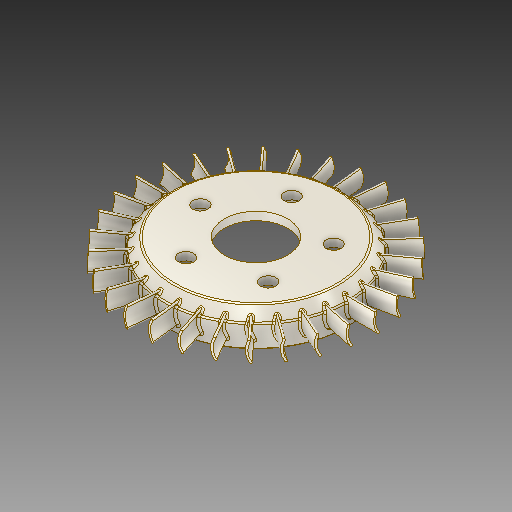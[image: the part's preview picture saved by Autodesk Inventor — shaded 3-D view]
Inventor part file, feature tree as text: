
AUTODESK INVENTOR PART (.ipt)
format: ipt  version: 2019 (Build 230136000, 136)  size: 2,094,080 bytes
history: native  units: mm
features: hole x4, sketch x4, extrude x3, fillet x3, chamfer x2, pattern_circular x2
ambient origin geometry x8: Origin, YZ Plane, XZ Plane, XY Plane, X Axis, Y Axis, Z Axis, Center Point
bodies: Solid1 (feature_tree)
feature tree (18):
  extrude  "Extrusion1"  Depth=26.0mm TaperAngle=0.0deg
  chamfer  "Chamfer1"  Distance=10.0mm
  fillet  "Fillet10"  Radius=44.0mm
  extrude  "Extrusion2"  Depth=19.5mm TaperAngle=360.0deg
  fillet  "Fillet2"  Radius=1.5mm
  pattern_circular  "Circular Pattern2"  Count=30  [1 undecoded]
  extrude  "Extrusion3"  Depth=19.5mm
  fillet  "Fillet1"  Radius=111.0mm
  hole  "Hole1"  [1 undecoded]
  hole  "Hole2"  [1 undecoded]
  hole  "Hole3"  [1 undecoded]
  pattern_circular  "Circular Pattern1"  [2 undecoded]
  hole  "Hole4"  [1 undecoded]
  chamfer  "Chamfer2"  Distance=2.0mm
  sketch  "Sketch1"  dims[d0=145.0mm d1=26.0mm d2=0.0mm]
  sketch  "Sketch2"  dims[d3=1.0mm]
  sketch  "Sketch3"  dims[d81=10.0mm d82=10.0mm d6=50.0mm d7=6.0mm d8=4.0mm d9=2.0mm d10=90.0deg d11=8.0mm d12=0.0mm d13=10.0mm d14=10.0mm]
  sketch  "Sketch4"  dims[d15=46.0mm d16=6.0mm d17=4.0mm d18=2.0mm d19=90.0deg d20=8.0mm d21=0.0mm d22=44.0mm d23=12.0mm d24=6.0mm d25=4.0mm d26=2.0mm d27=90.0deg d28=8.0mm d29=0.0mm d30=50.0mm d31=360.0deg d33=1.5mm d34=300.0mm d35=0.0mm d36=190.0mm d37=111.0mm d38=-0.523599mm d39=300.0mm d40=360.0deg d42=1.5mm d43=10.0mm d44=25.0mm d45=10.0mm d46=10.0mm d48=10.0mm d49=10.0mm d50=10.0mm d61=5.0mm d62=14.0mm d77=8.0mm d78=2.0mm d79=45.0deg d80=2.0mm d92=10.0mm d93=10.0mm d85=137.0mm d86=6.0mm d87=4.0mm d88=2.0mm d89=90.0deg d90=19.5mm d91=0.0mm d94=7.0mm d95=2.0mm d96=45.0deg]
note: 7 required parameter values undecoded (feature->parameter linkage not recoverable at this tier; creation-order binding heuristic only, values carry confidence <= 0.55)
